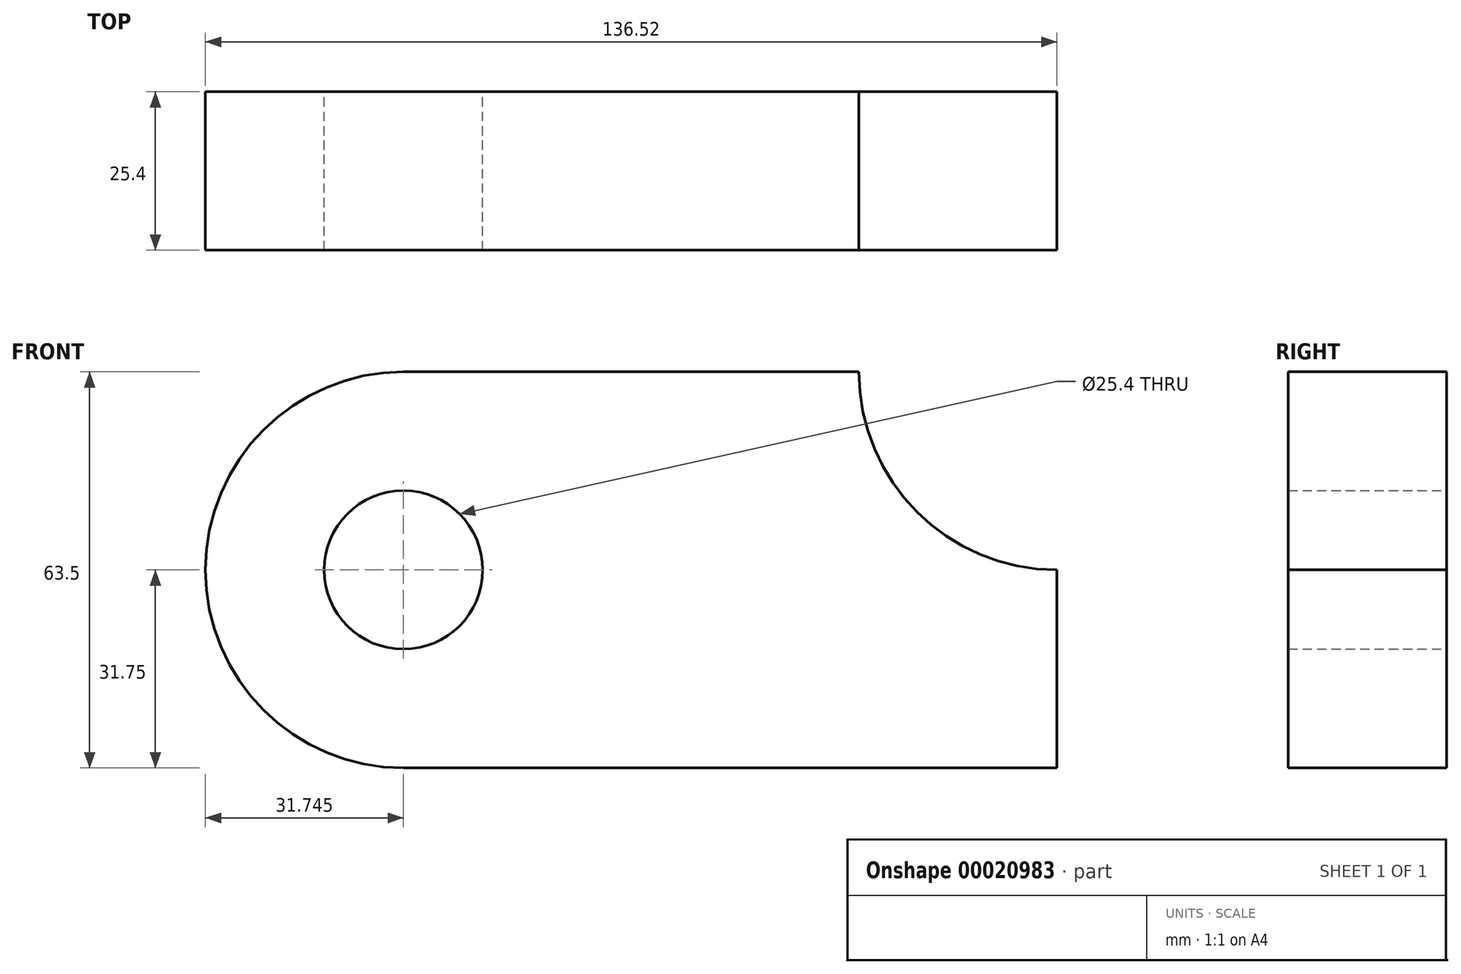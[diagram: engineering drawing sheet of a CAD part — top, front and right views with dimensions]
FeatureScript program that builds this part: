
annotation { "Feature Type Name" : "Feature", "Feature Type Description" : "" }
export const myFeature = defineFeature(function(context is Context, id is Id, definition is map)
    precondition{}
    {
        {
            var Q0;
            Q0=qCreatedBy(makeId("Front.planeOp"),FACE);
            var sketch = newSketch(context, id + "F0", { "sketchPlane" : qUnion([Q0])});
            skLineSegment(sketch, "E0.bottom", {"start": v(0, 0) * mm, "end": v(-104.77, 0) * mm});
            skLineSegment(sketch, "E0.top", {"start": v(-31.75, 63.5) * mm, "end": v(-104.77, 63.5) * mm});
            skLineSegment(sketch, "E0.left", {"start": v(0, 0) * mm, "end": v(0, 31.75) * mm});
            skArc(sketch, "E1", {"start": v(-104.77, 63.5) * mm, "mid": v(-136.52, 31.75) * mm, "end": v(-104.78, 0) * mm});
            skCircle(sketch, "E2", {"center": v(-104.77, 31.75) * mm, "radius": 12.7 * mm});
            skArc(sketch, "E3", {"start": v(-31.75, 63.5) * mm, "mid": v(-22.45, 41.05) * mm, "end": v(0, 31.75) * mm});
            skSolve(sketch);
        }
        {
            var Q0;
            Q0=makeQuery(id+"F0.imprint","IMPRINT",FACE,{"disambiguationData":[TD([[makeQuery(id+"F0.imprint","IMPRINT",EDGE,{"derivedFrom":sQuery(id+"F0.wireOp",EDGE,"E0.bottom")}),-1.0]])]});
            extrude(context, id + "F1", {"entities" : qUnion([Q0]), "depth" : 25.4 * mm});
        }
    });
